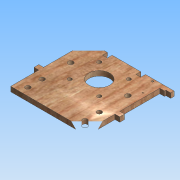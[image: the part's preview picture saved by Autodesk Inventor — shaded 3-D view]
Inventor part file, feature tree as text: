
AUTODESK INVENTOR PART (.ipt)
format: ipt  version: 2015 (Build 190159000, 159)  size: 300,032 bytes
history: native  units: mm
features: sketch x10, extrude x9, other x5, hole x3, projected_geometry x2, reference x2
ambient origin geometry x8: Origin, YZ Plane, XZ Plane, XY Plane, X Axis, Y Axis, Z Axis, Center Point
bodies: Body1 (feature_tree)
feature tree (31):
  other  "Blocks"
  extrude  "Extrusion2"  Depth=80.0mm
  hole  "Hole4"  [1 undecoded]
  hole  "Hole5"  [1 undecoded]
  hole  "Hole8"  [1 undecoded]
  extrude  "Extrusion11"  Depth=5.0mm
  extrude  "Extrusion12"  Depth=60.0mm
  extrude  "Extrusion13"  Depth=30.0mm
  sketch  "Sketch47"  dims[d78=22.0mm d79=6.0mm d80=4.0mm d81=2.0mm d82=90.0deg d83=2.0mm d84=0.0mm d176=28.0mm]
  extrude  "Extrusion14"  Depth=1.0mm
  extrude  "Extrusion15"  Depth=5.0mm
  extrude  "Extrusion16"  Depth=5.0mm TaperAngle=0.0deg
  extrude  "Extrusion17"  Depth=5.0mm TaperAngle=0.0deg
  extrude  "Extrusion18"  Depth=47.0mm
  sketch  "Sketch13"  dims[d21=80.0mm d22=50.0mm]
  sketch  "Sketch16"  dims[d23=5.0mm d24=0.0mm d43=31.0mm]
  sketch  "Sketch17"  dims[d44=31.0mm]
  other  "Block1"
  other  "Block2"
  other  "Block3"
  other  "Block4"
  projected_geometry  "Projected Loop3"
  sketch  "Sketch45"  dims[d45=4.0mm d46=6.0mm d47=4.0mm d48=2.0mm d49=90.0deg d50=4.0mm d51=0.0mm d52=60.0mm]
  projected_geometry  "Projected Loop4"
  reference  "Reference1"
  reference  "Reference2"
  sketch  "Sketch46"  dims[d53=5.2mm d54=6.0mm d55=4.0mm d56=2.0mm d57=90.0deg d58=4.0mm d59=0.0mm]
  sketch  "Sketch48"  dims[d179=5.0mm d184=5.0mm]
  sketch  "Sketch49"  dims[d185=8.0mm d189=60.0mm]
  sketch  "Sketch50"  dims[d190=30.0mm d191=8.0mm]
  sketch  "Sketch51"  dims[d192=5.0mm d193=15.0mm d196=5.0mm d197=5.0mm d198=0.0mm d200=5.0mm d201=0.0mm d202=47.0mm d203=5.0mm d204=5.0mm d205=20.0mm d206=5.0mm d207=5.0mm d208=20.0mm d209=10.0mm d210=0.0mm d211=2.0mm d212=2.5mm d213=10.0mm d214=2.0mm d215=10.0mm d216=2.5mm d217=10.0mm d218=0.0mm d219=10.0mm d220=0.0mm d221=5.0mm d222=5.0mm d223=5.0mm d224=5.0mm d225=5.0mm d226=0.0mm d227=5.0mm d228=5.0mm d229=47.0mm d230=5.0mm d231=0.0mm d232=5.0mm d233=5.0mm d234=47.0mm d235=5.0mm d236=0.0mm d29=1.0mm d30=1.0mm]
note: 3 required parameter values undecoded (feature->parameter linkage not recoverable at this tier; creation-order binding heuristic only, values carry confidence <= 0.55)
